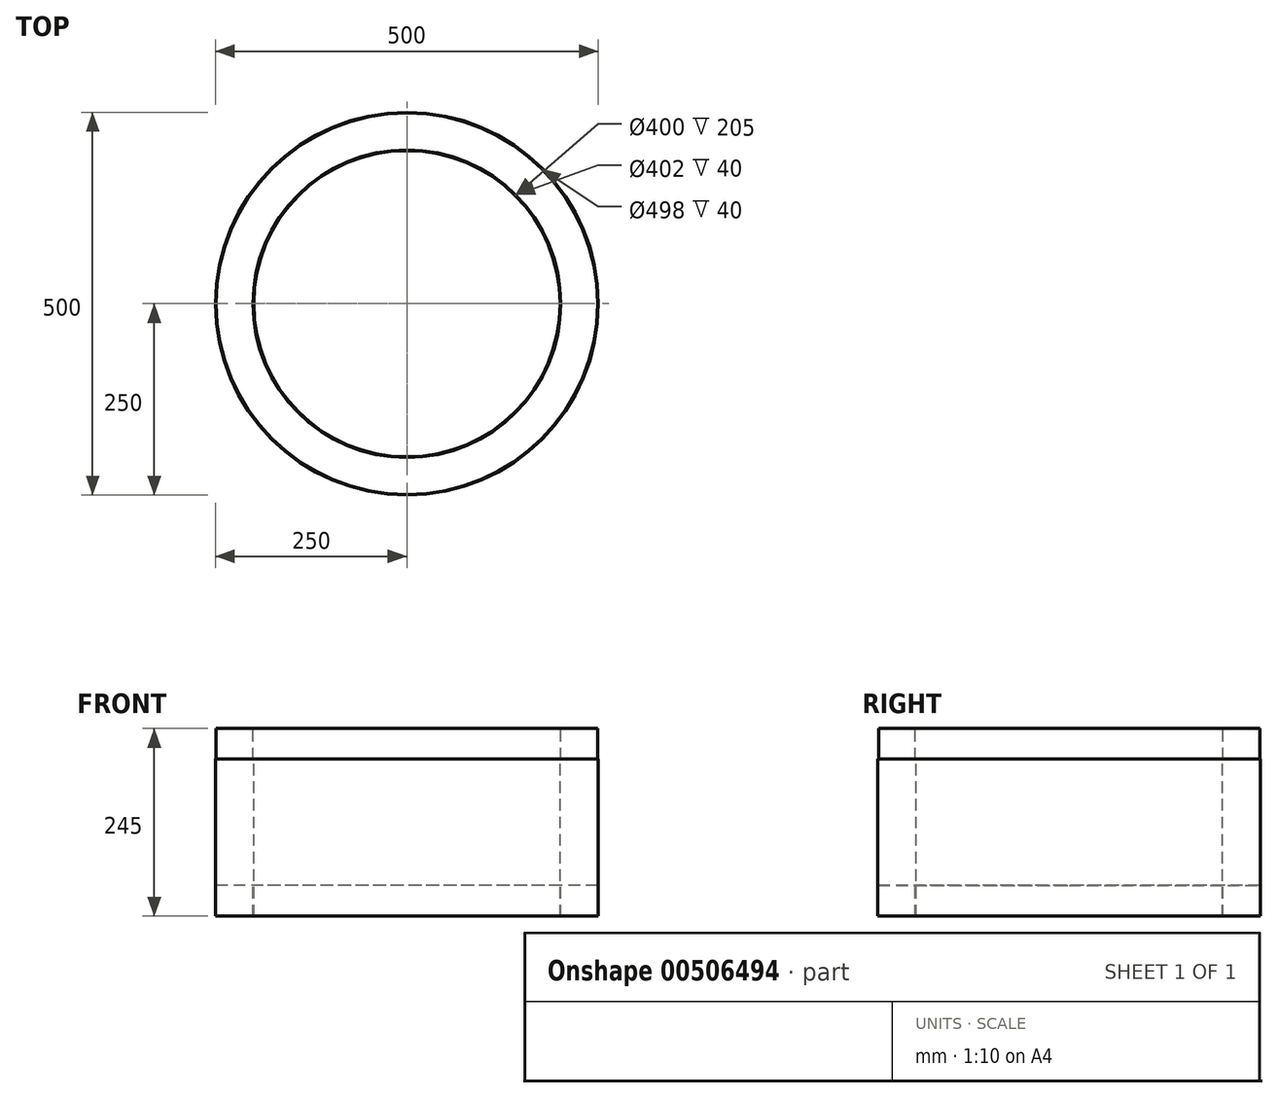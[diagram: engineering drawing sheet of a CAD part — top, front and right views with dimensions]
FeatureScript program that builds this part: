
annotation { "Feature Type Name" : "Feature", "Feature Type Description" : "" }
export const myFeature = defineFeature(function(context is Context, id is Id, definition is map)
    precondition{}
    {
        {
            var Q0;
            Q0=qCreatedBy(makeId("Front.planeOp"),FACE);
            var sketch = newSketch(context, id + "F0", { "sketchPlane" : qUnion([Q0])});
            skLineSegment(sketch, "E0", {"start": v(0, 74.87) * mm, "end": v(0, -73.71) * mm, "construction": true});
            skLineSegment(sketch, "E1", {"start": v(0, 374.84) * mm, "end": v(0, -528.94) * mm, "construction": true});
            skLineSegment(sketch, "E2", {"start": v(-200, -489.75) * mm, "end": v(-200, -284.75) * mm});
            skLineSegment(sketch, "E3", {"start": v(-200, -284.75) * mm, "end": v(-201, -284.75) * mm});
            skLineSegment(sketch, "E4", {"start": v(-201, -284.75) * mm, "end": v(-201, -244.75) * mm});
            skLineSegment(sketch, "E5", {"start": v(-201, -244.75) * mm, "end": v(-249, -244.75) * mm});
            skLineSegment(sketch, "E6", {"start": v(-249, -244.75) * mm, "end": v(-249, -284.75) * mm});
            skLineSegment(sketch, "E7", {"start": v(-249, -284.75) * mm, "end": v(-250, -284.75) * mm});
            skLineSegment(sketch, "E8", {"start": v(-250, -284.75) * mm, "end": v(-250, -489.75) * mm});
            skLineSegment(sketch, "E9", {"start": v(-250, -489.75) * mm, "end": v(-249, -489.75) * mm});
            skLineSegment(sketch, "E10", {"start": v(-249, -489.75) * mm, "end": v(-249, -449.75) * mm});
            skLineSegment(sketch, "E11", {"start": v(-249, -449.75) * mm, "end": v(-201, -449.75) * mm});
            skLineSegment(sketch, "E12", {"start": v(-201, -449.75) * mm, "end": v(-201, -489.75) * mm});
            skLineSegment(sketch, "E13", {"start": v(-201, -489.75) * mm, "end": v(-200, -489.75) * mm});
            skSolve(sketch);
        }
        {
            var Q0;
            Q0=qSketchRegion(id+"F0",true);
            var Q1;
            Q1=sQuery(id+"F0.wireOp",EDGE,"E1");
            revolve(context, id + "F1", {"entities" : qUnion([Q0]), "axis" : qUnion([Q1]), "revolveType" : RevolveType.FULL});
        }
    });
